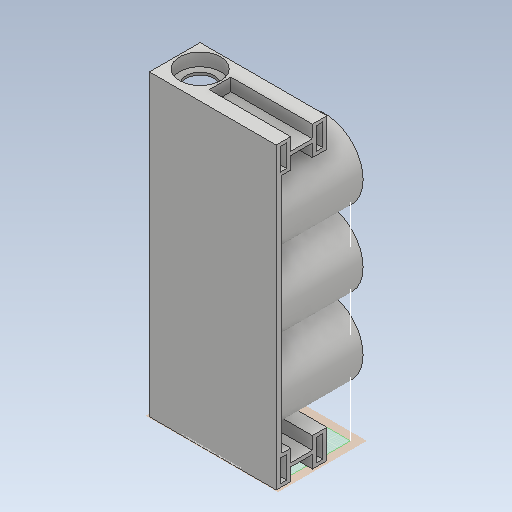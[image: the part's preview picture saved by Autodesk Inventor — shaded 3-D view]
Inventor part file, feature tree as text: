
AUTODESK INVENTOR PART (.ipt)
format: ipt  version: 2020 (Build 240168000, 168)  size: 861,184 bytes
history: native  units: mm
features: sketch x32, extrude x29, fillet x6
ambient origin geometry x8: Origin, YZ Plane, XZ Plane, XY Plane, X Axis, Y Axis, Z Axis, Center Point
bodies: Solid1 (feature_tree)
feature tree (67):
  extrude  "Extrusion1"  Depth=165.0mm
  extrude  "Extrusion2"  Depth=8.5mm
  extrude  "Extrusion3"  Depth=25.0mm TaperAngle=0.0deg
  extrude  "Extrusion4"  Depth=25.0mm
  extrude  "Extrusion5"  Depth=7.1mm
  extrude  "Extrusion6"  Depth=7.1mm TaperAngle=0.0deg
  fillet  "Fillet1"  Radius=5.0mm
  extrude  "Extrusion7"  Depth=10.0mm TaperAngle=0.0deg
  fillet  "Fillet2"  Radius=2.0mm
  extrude  "Extrusion8"  Depth=8.0mm
  extrude  "Extrusion9"  Depth=16.0mm
  fillet  "Fillet3"  Radius=8.0mm
  extrude  "Extrusion10"  Depth=6.0mm
  extrude  "Extrusion11"  Depth=3.5mm
  sketch  "Sketch12"  dims[d32=12.25mm d33=3.5mm]
  sketch  "Sketch13"  dims[d34=12.25mm d35=12.25mm]
  extrude  "Extrusion12"  Depth=3.5mm
  extrude  "Extrusion13"  Depth=12.25mm
  sketch  "Sketch16"  dims[d41=8.0mm d42=1.0mm]
  extrude  "Extrusion14"  Depth=40.0mm TaperAngle=0.0deg
  extrude  "Extrusion15"  Depth=2.0mm
  extrude  "Extrusion16"  Depth=1.0mm
  extrude  "Extrusion17"  Depth=2.0mm TaperAngle=0.0deg
  extrude  "Extrusion18"  Depth=7.1mm TaperAngle=0.0deg
  fillet  "Fillet4"  Radius=3.0mm
  extrude  "Extrusion19"  Depth=42.0mm
  extrude  "Extrusion20"  Depth=42.0mm
  extrude  "Extrusion21"  Depth=42.0mm
  extrude  "Extrusion22"  Depth=2.0mm
  extrude  "Extrusion23"  Depth=2.0mm
  extrude  "Extrusion24"  Depth=45.0mm TaperAngle=0.0deg
  fillet  "Fillet5"  Radius=10.0mm
  extrude  "Extrusion25"  Depth=2.0mm TaperAngle=0.0deg
  fillet  "Fillet6"  Radius=2.0mm
  extrude  "Extrusion26"  Depth=2.0mm
  extrude  "Extrusion27"  Depth=2.0mm
  extrude  "Extrusion28"  Depth=7.0mm TaperAngle=0.0deg
  extrude  "Extrusion29"  Depth=1.0mm
  sketch  "Sketch1"  dims[d0=25.0mm d1=165.0mm]
  sketch  "Sketch2"  dims[d2=3.0mm d3=0.0mm d4=8.5mm]
  sketch  "Sketch3"  dims[d5=8.5mm d6=25.0mm d7=0.0mm]
  sketch  "Sketch4"  dims[d8=25.0mm d9=22.75mm]
  sketch  "Sketch5"  dims[d10=7.1mm d11=0.0mm d12=15.5mm]
  sketch  "Sketch6"  dims[d13=165.0mm d14=0.0mm d15=7.1mm d16=0.0mm d17=5.0mm]
  sketch  "Sketch7"  dims[d18=5.0mm d19=10.0mm d20=0.0mm d21=2.0mm]
  sketch  "Sketch8"  dims[d22=16.0mm d23=8.0mm]
  sketch  "Sketch9"  dims[d24=16.0mm d25=16.0mm d26=8.0mm]
  sketch  "Sketch10"  dims[d27=45.0mm d28=0.0mm d29=6.0mm]
  sketch  "Sketch11"  dims[d30=12.25mm d31=3.5mm]
  sketch  "Sketch14"  dims[d36=3.5mm d37=40.0mm d38=0.0mm]
  sketch  "Sketch15"  dims[d39=1.0mm d40=2.0mm]
  sketch  "Sketch17"  dims[d43=2.0mm d44=12.0mm d45=0.0mm]
  sketch  "Sketch18"  dims[d46=6.0mm d47=7.1mm d48=0.0mm d49=3.0mm d50=0.0mm]
  sketch  "Sketch19"  dims[d51=42.0mm d52=38.75mm]
  sketch  "Sketch20"  dims[d53=42.0mm d54=38.75mm]
  sketch  "Sketch21"  dims[d55=42.0mm d56=38.75mm]
  sketch  "Sketch22"  dims[d57=45.0mm d58=0.0mm d59=2.0mm]
  sketch  "Sketch23"  dims[d60=4.0mm d61=2.0mm]
  sketch  "Sketch24"  dims[d62=4.0mm d63=45.0mm d64=0.0mm d65=10.0mm]
  sketch  "Sketch25"  dims[d66=12.0mm d67=0.0mm d68=2.0mm d69=0.0mm d70=2.0mm d71=0.0mm]
  sketch  "Sketch26"  dims[d72=2.0mm d73=2.0mm]
  sketch  "Sketch27"  dims[d74=5.0mm d75=0.0mm d76=2.0mm]
  sketch  "Sketch28"  dims[d77=2.0mm d78=7.0mm d79=0.0mm]
  sketch  "Sketch29"  dims[d80=1.0mm d81=0.25mm]
  sketch  "Sketch30"  dims[d82=0.25mm]
  sketch  "Sketch31"  dims[d83=44.75mm d84=0.0mm]
  sketch  "Sketch32"  dims[d85=44.0mm d86=0.0mm d87=22.6mm d88=8.5mm d89=0.0mm d90=22.6mm d91=8.5mm d92=0.0mm d93=27.0mm d94=0.0mm d95=60.0mm d96=19.05mm d97=3.0mm d98=0.0mm d99=31.75mm d100=19.05mm d101=19.05mm d102=31.5mm d103=0.0mm d104=38.0mm d105=12.954mm d106=27.5mm d107=0.0mm d108=18.0mm d109=18.0mm d110=18.0mm d111=18.0mm d112=18.0mm d113=0.0mm d114=2.0mm d115=2.0mm d116=2.0mm d117=5.0mm d118=0.0mm d119=10.0mm d120=148.0mm d121=0.0mm]
